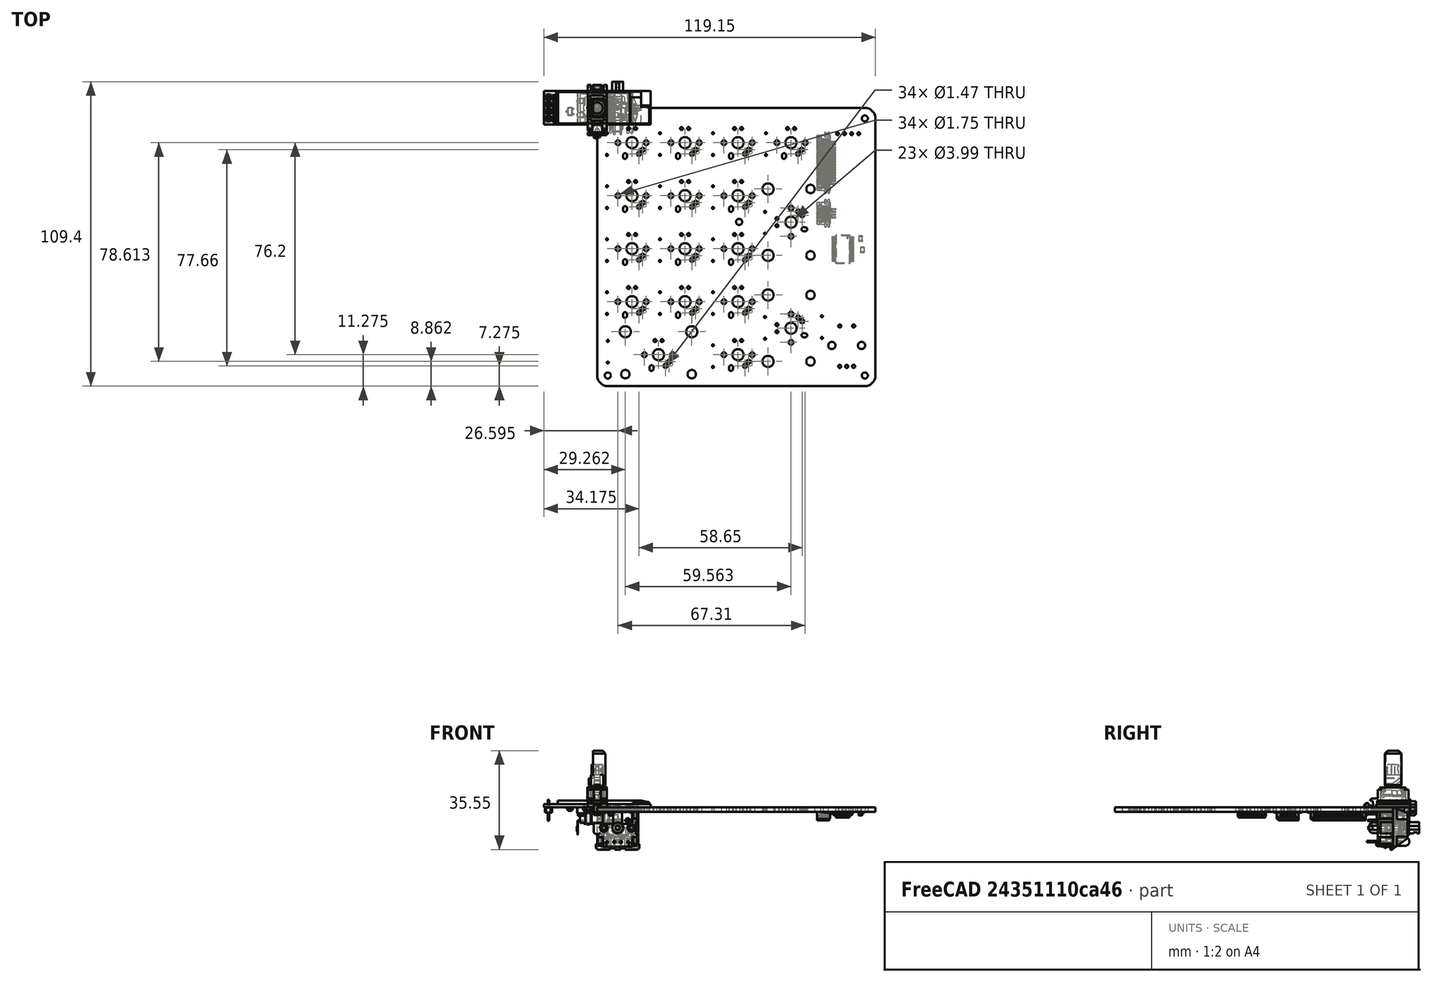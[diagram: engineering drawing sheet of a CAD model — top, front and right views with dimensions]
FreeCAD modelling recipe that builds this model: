
FCSTD DOCUMENT  (FreeCAD 0.19R24267 (Git))
Label: quartet_matrix_numpad
License: All rights reserved
LicenseURL: http://en.wikipedia.org/wiki/All_rights_reserved
objects: Part::Feature×36, App::Link×36, App::Part×13, PartDesign::CoordinateSystem×1, Sketcher::SketchObject×1
note: 38 computed .brp shape members not serialized (recipe doc carries the construction recipe); baked Part::Feature solids carry a one-line shape summary decoded from their .brp

FEATURE [PartDesign::CoordinateSystem] Local_CS_ec40
  AttacherType = Attacher::AttachEngine3D
FEATURE [Part::Feature] Pcb_ec40
  shape: bbox 100 x 100 x 1.6 mm, 259 faces (baked)
FEATURE [Sketcher::SketchObject] PCB_Sketch_ec40
  FullyConstrained = false
  sketch-geometry (8):
    g0: LineSegment StartX=3.81 StartY=-4e-16 StartZ=0 EndX=96.19 EndY=9.3e-15 EndZ=0
    g1: LineSegment StartX=100 StartY=-3.81 StartZ=0 EndX=100 EndY=-96.19 EndZ=0
    g2: LineSegment StartX=96.19 StartY=-100 StartZ=0 EndX=3.81 EndY=-100 EndZ=0
    g3: LineSegment StartX=-7.5e-15 StartY=-96.19 StartZ=0 EndX=4e-16 EndY=-3.81 EndZ=0
    g4: ArcOfCircle CenterX=3.81 CenterY=-3.81 CenterZ=0 NormalX=0 NormalY=0 NormalZ=1 AngleXU=0 Radius=3.81 StartAngle=1.5708 EndAngle=3.14159
    g5: ArcOfCircle CenterX=3.81 CenterY=-96.19 CenterZ=0 NormalX=0 NormalY=0 NormalZ=1 AngleXU=0 Radius=3.81 StartAngle=3.14159 EndAngle=4.71239
    g6: ArcOfCircle CenterX=96.19 CenterY=-96.19 CenterZ=0 NormalX=0 NormalY=0 NormalZ=1 AngleXU=0 Radius=3.81 StartAngle=4.71239 EndAngle=6.28319
    g7: ArcOfCircle CenterX=96.19 CenterY=-3.81 CenterZ=0 NormalX=0 NormalY=0 NormalZ=1 AngleXU=0 Radius=3.81 StartAngle=0 EndAngle=1.5708
  constraints (8):
    c: Coincident(g3,g5)
    c: Coincident(g3,g4)
    c: Coincident(g2,g5)
    c: Coincident(g0,g4)
    c: Coincident(g2,g6)
    c: Coincident(g0,g7)
    c: Coincident(g1,g6)
    c: Coincident(g1,g7)
FEATURE [App::Part] Board_Geoms_ec40
  Group = -> [Local_CS_ec40,Pcb_ec40,PCB_Sketch_ec40]
  Origin = -> Origin
FEATURE [Part::Feature] Part__Feature  label="MX Top Housing"
  shape: bbox 14.82 x 9.998 x 14.77 mm, 582 faces (baked)
FEATURE [Part::Feature] Part__Feature001  label="MX Bottom Housing"
  Placement = pos=(7.35,-0.2,-7.35) rot=(0,0,1;0rad)
  shape: bbox 15.74 x 12.51 x 15.74 mm, 598 faces (baked)
FEATURE [App::Part] Housing
  Group = -> [Part__Feature,Part__Feature001]
  Origin = -> Origin008
  Placement = pos=(7.35,7.35,6) rot=(0,0.707107,0.707107;3.14159rad)
FEATURE [Part::Feature] Part__Feature002  label="MX Slider"
  Placement = pos=(7.35,2,-7.35) rot=(0,0,1;0rad)
  shape: bbox 8.9 x 10.4 x 5.7 mm, 279 faces (baked)
FEATURE [App::Part] Slider
  Group = -> [Part__Feature002]
  Origin = -> Origin009
  Placement = pos=(7.35,7.35,6) rot=(0,0.707107,0.707107;3.14159rad)
FEATURE [Part::Feature] Part__Feature003  label="MX Pins"
  Placement = pos=(-5.57275,-8.7,12.741) rot=(0,0,1;0rad)
  shape: bbox 7.319 x 6.711 x 2.971 mm, 35 faces, 2 solids (baked)
FEATURE [App::Part] Pins
  Group = -> [Part__Feature003]
  Origin = -> Origin010
  Placement = pos=(7.35,7.35,6) rot=(0,0.707107,0.707107;3.14159rad)
FEATURE [Part::Feature] Part__Feature004  label="MX LED"
  Placement = pos=(7.35,0.5,-12.292) rot=(0,0,1;0rad)
  shape: bbox 3.003 x 15.3 x 3.003 mm, 33 faces, 5 solids (baked)
FEATURE [App::Part] LED
  Group = -> [Part__Feature004]
  Origin = -> Origin011
  Placement = pos=(7.35,7.35,6) rot=(0,0.707107,0.707107;3.14159rad)
FEATURE [App::Part] Switch_v7  label="K_PGUP_0_Switch v7_7FFFFFFF"
  Group = -> [Housing,Slider,Pins,LED]
  Origin = -> Origin012
  Placement = pos=(50.625,-31.575,0) rot=(0,0,1;3.14159rad)
FEATURE [Part::Feature] Shape  label="J2_F519-1A7A1-11016-E200_5FF7934A"
  Placement = pos=(78.966,-12.74,-1.6) rot=(0,0,1;1.5708rad)
  shape: bbox 6.803 x 22 x 3.003 mm, 1188 faces (baked)
FEATURE [Part::Feature] Shape001  label="J2_F519-1A7A1-11004-E200_5FF7934A[2]"
  Placement = pos=(78.966,-24.87,-1.6) rot=(0,0,1;1.5708rad)
  shape: bbox 6.803 x 10 x 3.003 mm, 509 faces (baked)
FEATURE [Part::Feature] Shape002  label="U2_SSOP_28_53x102mm_P065mm_5FF8A5C0"
  Placement = pos=(88.265,-50.8,-1.6) rot=(0,1,0;3.14159rad)
  shape: bbox 7.8 x 10.2 x 2.1 mm, 456 faces (baked)
FEATURE [App::Link] U2_SSOP_28_53x102mm_P065mm_5FF8A5C0_ln_  label="U1_SSOP_28_53x102mm_P065mm_5FF8A58F"
  LinkPlacement = pos=(68.58,-59.69,-1.6) rot=(0.707107,0.707107,0;3.14159rad)
  LinkedObject = -> Shape002
  Placement = pos=(68.58,-59.69,-1.6) rot=(0.707107,0.707107,0;3.14159rad)
FEATURE [Part::Feature] Part__Feature005  label="482020714001"
  shape: bbox 13.75 x 11.7 x 25.9 mm, 186 faces (baked)
FEATURE [Part::Feature] Part__Feature006  label="pin"
  Placement = pos=(7.6,-2.5,-2.5) rot=(0,0,1;1.5708rad)
  shape: bbox 2.15 x 1.5 x 7.2 mm, 14 faces (baked)
FEATURE [Part::Feature] Part__Feature007  label="pin_short"
  Placement = pos=(-7.1,-2.5,-4.7) rot=(0,0,-1;1.5708rad)
  shape: bbox 2.353 x 1.503 x 5.003 mm, 32 faces (baked)
FEATURE [Part::Feature] Part__Feature008  label="contact_plate"
  Placement = pos=(2e-16,0,-5.9) rot=(0,0,-1;1.5708rad)
  shape: bbox 9.516 x 11.61 x 9.056 mm, 134 faces (baked)
FEATURE [Part::Feature] Part__Feature009  label="pin001"
  Placement = pos=(7.6,2.5,-2.5) rot=(0,0,1;1.5708rad)
  shape: bbox 2.15 x 1.5 x 7.2 mm, 14 faces (baked)
FEATURE [Part::Feature] Part__Feature010  label="pin002"
  Placement = pos=(7.6,-1.04e-14,-2.5) rot=(0,0,1;1.5708rad)
  shape: bbox 2.15 x 1.5 x 7.2 mm, 14 faces (baked)
FEATURE [Part::Feature] Part__Feature011  label="pin_short001"
  Placement = pos=(-7.1,2.5,-4.7) rot=(0,0,-1;1.5708rad)
  shape: bbox 2.353 x 1.503 x 5.003 mm, 32 faces (baked)
FEATURE [App::Part] _820xx514001_v1  label="SW1_4820xx514001 v1_5FF8A8AA"
  Group = -> [Part__Feature005,Part__Feature006,Part__Feature007,Part__Feature008,Part__Feature009,Part__Feature010,Part__Feature011]
  Origin = -> Origin013
  Placement = pos=(89.67,-85.4,6) rot=(0,0,-1;1.5708rad)
FEATURE [Part::Feature] Shape003  label="R12_R_0805_2012Metric_5FF8A528"
  Placement = pos=(95.25,-51.045,-1.6) rot=(-0.707107,0.707107,0;3.14159rad)
  shape: bbox 1.2 x 2 x 0.45 mm, 26 faces (baked)
FEATURE [App::Link] R12_R_0805_2012Metric_5FF8A528_ln_  label="R11_R_0805_2012Metric_5FF8A517"
  LinkPlacement = pos=(90.424,-21.336,-1.6) rot=(1,0,0;3.14159rad)
  LinkedObject = -> Shape003
  Placement = pos=(90.424,-21.336,-1.6) rot=(1,0,0;3.14159rad)
FEATURE [App::Link] R12_R_0805_2012Metric_5FF8A528_ln_001  label="R10_R_0805_2012Metric_5FF8A506"
  LinkPlacement = pos=(90.424,-19.304,-1.6) rot=(1,0,0;3.14159rad)
  LinkedObject = -> Shape003
  Placement = pos=(90.424,-19.304,-1.6) rot=(1,0,0;3.14159rad)
FEATURE [App::Link] R12_R_0805_2012Metric_5FF8A528_ln_002  label="R9_R_0805_2012Metric_5FF8A4F5"
  LinkPlacement = pos=(90.433,-17.272,-1.6) rot=(1,0,0;3.14159rad)
  LinkedObject = -> Shape003
  Placement = pos=(90.433,-17.272,-1.6) rot=(1,0,0;3.14159rad)
FEATURE [App::Link] R12_R_0805_2012Metric_5FF8A528_ln_003  label="R8_R_0805_2012Metric_5FF8A4E4"
  LinkPlacement = pos=(90.433,-15.24,-1.6) rot=(1,0,0;3.14159rad)
  LinkedObject = -> Shape003
  Placement = pos=(90.433,-15.24,-1.6) rot=(1,0,0;3.14159rad)
FEATURE [App::Link] R12_R_0805_2012Metric_5FF8A528_ln_004  label="R7_R_0805_2012Metric_5FF8A4D3"
  LinkPlacement = pos=(71.628,-51.807,-1.6) rot=(0.707107,0.707107,0;3.14159rad)
  LinkedObject = -> Shape003
  Placement = pos=(71.628,-51.807,-1.6) rot=(0.707107,0.707107,0;3.14159rad)
FEATURE [App::Link] R12_R_0805_2012Metric_5FF8A528_ln_005  label="R6_R_0805_2012Metric_5FF8A4C2"
  LinkPlacement = pos=(69.596,-51.807,-1.6) rot=(0.707107,0.707107,0;3.14159rad)
  LinkedObject = -> Shape003
  Placement = pos=(69.596,-51.807,-1.6) rot=(0.707107,0.707107,0;3.14159rad)
FEATURE [App::Link] R12_R_0805_2012Metric_5FF8A528_ln_006  label="R5_R_0805_2012Metric_5FF8A4B1"
  LinkPlacement = pos=(67.564,-51.807,-1.6) rot=(0.707107,0.707107,0;3.14159rad)
  LinkedObject = -> Shape003
  Placement = pos=(67.564,-51.807,-1.6) rot=(0.707107,0.707107,0;3.14159rad)
FEATURE [App::Link] R12_R_0805_2012Metric_5FF8A528_ln_007  label="R4_R_0805_2012Metric_5FF8A4A0"
  LinkPlacement = pos=(65.532,-51.816,-1.6) rot=(0.707107,0.707107,0;3.14159rad)
  LinkedObject = -> Shape003
  Placement = pos=(65.532,-51.816,-1.6) rot=(0.707107,0.707107,0;3.14159rad)
FEATURE [App::Link] R12_R_0805_2012Metric_5FF8A528_ln_008  label="R3_R_0805_2012Metric_5FF917EF"
  LinkPlacement = pos=(67.056,-67.047,-1.6) rot=(0.707107,0.707107,0;3.14159rad)
  LinkedObject = -> Shape003
  Placement = pos=(67.056,-67.047,-1.6) rot=(0.707107,0.707107,0;3.14159rad)
FEATURE [App::Link] R12_R_0805_2012Metric_5FF8A528_ln_009  label="R2_R_0805_2012Metric_5FF8A47E"
  LinkPlacement = pos=(97.536,-91.431,0) rot=(0,0,1;1.5708rad)
  LinkedObject = -> Shape003
  Placement = pos=(97.536,-91.431,0) rot=(0,0,1;1.5708rad)
FEATURE [App::Link] R12_R_0805_2012Metric_5FF8A528_ln_010  label="R1_R_0805_2012Metric_5FF8A46D"
  LinkPlacement = pos=(81.788,-91.957,0) rot=(0,0,-1;1.5708rad)
  LinkedObject = -> Shape003
  Placement = pos=(81.788,-91.957,0) rot=(0,0,-1;1.5708rad)
FEATURE [Part::Feature] Shape004  label="C4_C_0805_2012Metric_5FF89E4F"
  Placement = pos=(94.615,-46.99,-1.6) rot=(-0.707107,0.707107,0;3.14159rad)
  shape: bbox 1.25 x 2 x 1.25 mm, 28 faces (baked)
FEATURE [App::Link] C4_C_0805_2012Metric_5FF89E4F_ln_  label="C3_C_0805_2012Metric_5FF90FF2"
  LinkPlacement = pos=(96.647,-46.99,-1.6) rot=(-0.707107,0.707107,0;3.14159rad)
  LinkedObject = -> Shape004
  Placement = pos=(96.647,-46.99,-1.6) rot=(-0.707107,0.707107,0;3.14159rad)
FEATURE [App::Link] C4_C_0805_2012Metric_5FF89E4F_ln_001  label="C2_C_0805_2012Metric_5FF9E241"
  LinkPlacement = pos=(71.12,-67.047,-1.6) rot=(0.707107,0.707107,0;3.14159rad)
  LinkedObject = -> Shape004
  Placement = pos=(71.12,-67.047,-1.6) rot=(0.707107,0.707107,0;3.14159rad)
FEATURE [App::Link] C4_C_0805_2012Metric_5FF89E4F_ln_002  label="C1_C_0805_2012Metric_5FF9E2B4"
  LinkPlacement = pos=(69.088,-67.047,-1.6) rot=(0.707107,0.707107,0;3.14159rad)
  LinkedObject = -> Shape004
  Placement = pos=(69.088,-67.047,-1.6) rot=(0.707107,0.707107,0;3.14159rad)
FEATURE [App::Part] Bot_ec40
  Group = -> [Shape,Shape001,Shape002,U2_SSOP_28_53x102mm_P065mm_5FF8A5C0_ln_,Shape003,R12_R_0805_2012Metric_5FF8A528_ln_,R12_R_0805_2012Metric_5FF8A528_ln_001,R12_R_0805_2012Metric_5FF8A528_ln_002,R12_R_0805_2012Metric_5FF8A528_ln_003,R12_R_0805_2012Metric_5FF8A528_ln_004,R12_R_0805_2012Metric_5FF8A528_ln_005,R12_R_0805_2012Metric_5FF8A528_ln_006,R12_R_0805_2012Metric_5FF8A528_ln_007,+5 more]
  Origin = -> Origin004
FEATURE [Part::Feature] Part__Feature012  label="OLED_0.91_128x32.stp"
  shape: bbox 38.3 x 12.1 x 2.57 mm, 270 faces (baked)
FEATURE [Part::Feature] Part__Feature013  label="RESC-0603.stp"
  Placement = pos=(4.3,-5.3,0) rot=(1,0,0;3.14159rad)
  shape: bbox 1.7 x 0.9 x 0.55 mm, 52 faces, 3 solids (baked)
FEATURE [Part::Feature] Part__Feature014  label="RESC-0603.stp001"
  Placement = pos=(4.3,-3.8,0) rot=(1,0,0;3.14159rad)
  shape: bbox 1.7 x 0.9 x 0.55 mm, 52 faces, 3 solids (baked)
FEATURE [Part::Feature] Part__Feature015  label="RESC-0603.stp002"
  Placement = pos=(4.3,-2.3,0) rot=(1,0,0;3.14159rad)
  shape: bbox 1.7 x 0.9 x 0.55 mm, 52 faces, 3 solids (baked)
FEATURE [Part::Feature] Part__Feature016  label="RESC-0603.stp003"
  Placement = pos=(4.3,-0.8,0) rot=(1,0,0;3.14159rad)
  shape: bbox 1.7 x 0.9 x 0.55 mm, 52 faces, 3 solids (baked)
FEATURE [Part::Feature] Part__Feature017  label="RESC-0603.stp004"
  Placement = pos=(4.3,0.7,0) rot=(1,0,0;3.14159rad)
  shape: bbox 1.7 x 0.9 x 0.55 mm, 52 faces, 3 solids (baked)
FEATURE [Part::Feature] Part__Feature018  label="RESC-0603.stp005"
  Placement = pos=(4.3,2.2,0) rot=(1,0,0;3.14159rad)
  shape: bbox 1.7 x 0.9 x 0.55 mm, 52 faces, 3 solids (baked)
FEATURE [Part::Feature] Part__Feature019  label="RESC-0603.stp006"
  Placement = pos=(4.3,3.7,0) rot=(1,0,0;3.14159rad)
  shape: bbox 1.7 x 0.9 x 0.55 mm, 52 faces, 3 solids (baked)
FEATURE [Part::Feature] Part__Feature020  label="RESC-0603.stp007"
  Placement = pos=(4.3,5.2,0) rot=(1,0,0;3.14159rad)
  shape: bbox 1.7 x 0.9 x 0.55 mm, 52 faces, 3 solids (baked)
FEATURE [Part::Feature] Part__Feature021  label="RESC-0603.stp008"
  Placement = pos=(-1.4,-3.06,0) rot=(1,0,0;3.14159rad)
  shape: bbox 1.7 x 0.9 x 0.55 mm, 52 faces, 3 solids (baked)
FEATURE [Part::Feature] Part__Feature022  label="RESC-0603.stp009"
  Placement = pos=(-1.4,-1.56,0) rot=(1,0,0;3.14159rad)
  shape: bbox 1.7 x 0.9 x 0.55 mm, 52 faces, 3 solids (baked)
FEATURE [Part::Feature] Part__Feature023  label="RESC-0603.stp010"
  Placement = pos=(-1.4,-0.06,0) rot=(1,0,0;3.14159rad)
  shape: bbox 1.7 x 0.9 x 0.55 mm, 52 faces, 3 solids (baked)
FEATURE [Part::Feature] Part__Feature024  label="RESC-0603.stp011"
  Placement = pos=(-1.4,1.44,0) rot=(1,0,0;3.14159rad)
  shape: bbox 1.7 x 0.9 x 0.55 mm, 52 faces, 3 solids (baked)
FEATURE [Part::Feature] Part__Feature025  label="RESC-0603.stp012"
  Placement = pos=(-1.4,2.94,0) rot=(1,0,0;3.14159rad)
  shape: bbox 1.7 x 0.9 x 0.55 mm, 52 faces, 3 solids (baked)
FEATURE [Part::Feature] Part__Feature026  label="2SD0601A.stp"
  Placement = pos=(-9.8,-1.3,-0.08) rot=(-1,0,0;1.5708rad)
  shape: bbox 2.759 x 2.9 x 1.18 mm, 55 faces, 4 solids (baked)
FEATURE [Part::Feature] Part__Feature027  label="pcb_connector_350-80-104-00-019101"
  Placement = pos=(-17.55,1.9e-15,-0.06) rot=(0.57735,0.57735,-0.57735;4.18879rad)
  shape: bbox 2.54 x 10.16 x 7.644 mm, 74 faces (baked)
FEATURE [App::Part] SSD1306_OLED_0_91_128x32_SHORT_HEADER_v2  label="A1_SSD1306_OLED_0.91_128x32_SHORT_HEADER v2_5FF7990D"
  Group = -> [Part__Feature012,Part__Feature013,Part__Feature014,Part__Feature015,Part__Feature016,Part__Feature017,Part__Feature018,Part__Feature019,Part__Feature020,Part__Feature021,Part__Feature022,Part__Feature023,Part__Feature024,Part__Feature025,Part__Feature026,Part__Feature027]
  Origin = -> Origin014
  Placement = pos=(90.185,-26.78,1.9) rot=(0,0,-1;1.5708rad)
FEATURE [App::Link] K_PGUP_0_Switch_v7_7FFFFFFF_ln_  label="K_UP_0_PGUP_0_Switch v7_7FFFFFFF"
  LinkPlacement = pos=(31.575,-31.575,0) rot=(0,0,1;3.14159rad)
  LinkedObject = -> Switch_v7
  Placement = pos=(31.575,-31.575,0) rot=(0,0,1;3.14159rad)
FEATURE [App::Link] K_PGUP_0_Switch_v7_7FFFFFFF_ln_001  label="K_SLASH_0_PGUP_0_Switch v7_7FFFFFFF"
  LinkPlacement = pos=(31.575,-12.525,0) rot=(0,0,1;3.14159rad)
  LinkedObject = -> Switch_v7
  Placement = pos=(31.575,-12.525,0) rot=(0,0,1;3.14159rad)
FEATURE [App::Link] K_PGUP_0_Switch_v7_7FFFFFFF_ln_002  label="K_RIGHT_0_PGUP_0_Switch v7_7FFFFFFF"
  LinkPlacement = pos=(50.625,-50.625,0) rot=(0,0,1;3.14159rad)
  LinkedObject = -> Switch_v7
  Placement = pos=(50.625,-50.625,0) rot=(0,0,1;3.14159rad)
FEATURE [App::Link] K_PGUP_0_Switch_v7_7FFFFFFF_ln_003  label="K_PGDN_0_PGUP_0_Switch v7_7FFFFFFF"
  LinkPlacement = pos=(50.625,-69.675,0) rot=(0,0,1;3.14159rad)
  LinkedObject = -> Switch_v7
  Placement = pos=(50.625,-69.675,0) rot=(0,0,1;3.14159rad)
FEATURE [App::Link] K_PGUP_0_Switch_v7_7FFFFFFF_ln_004  label="K_NUM_LOCK_0_PGUP_0_Switch v7_7FFFFFFF"
  LinkPlacement = pos=(12.525,-12.525,0) rot=(0,0,1;3.14159rad)
  LinkedObject = -> Switch_v7
  Placement = pos=(12.525,-12.525,0) rot=(0,0,1;3.14159rad)
FEATURE [App::Link] K_PGUP_0_Switch_v7_7FFFFFFF_ln_005  label="K_MINUS_0_PGUP_0_Switch v7_7FFFFFFF"
  LinkPlacement = pos=(69.675,-12.525,0) rot=(0,0,1;3.14159rad)
  LinkedObject = -> Switch_v7
  Placement = pos=(69.675,-12.525,0) rot=(0,0,1;3.14159rad)
FEATURE [App::Link] K_PGUP_0_Switch_v7_7FFFFFFF_ln_006  label="K_LEFT_0_PGUP_0_Switch v7_7FFFFFFF"
  LinkPlacement = pos=(12.525,-50.625,0) rot=(0,0,1;3.14159rad)
  LinkedObject = -> Switch_v7
  Placement = pos=(12.525,-50.625,0) rot=(0,0,1;3.14159rad)
FEATURE [App::Link] K_PGUP_0_Switch_v7_7FFFFFFF_ln_007  label="K_INS_0_PGUP_0_Switch v7_7FFFFFFF"
  LinkPlacement = pos=(22.05,-88.725,0) rot=(0,0,1;3.14159rad)
  LinkedObject = -> Switch_v7
  Placement = pos=(22.05,-88.725,0) rot=(0,0,1;3.14159rad)
FEATURE [Part::Feature] Part__Feature028  label="mx Stabilizer base 16828"
  Placement = pos=(0,-1.1e-15,3.6) rot=(1,0,0;1.5708rad)
  shape: bbox 6.814 x 19.68 x 10.11 mm, 157 faces (baked)
FEATURE [Part::Feature] Part__Feature029  label="mx Stabilizer key 16828"
  Placement = pos=(0,-3.3e-15,11.7) rot=(1,0,0;1.5708rad)
  shape: bbox 4.613 x 8.314 x 11.98 mm, 287 faces (baked)
FEATURE [App::Part] Cherry_MX_Stabilizer_Open_v1  label="K_INS_0_Cherry MX Stabilizer Open v1_7FFFFFFF[2]"
  Group = -> [Part__Feature028,Part__Feature029]
  Origin = -> Origin015
  Placement = pos=(33.988,-88.725,0) rot=(0,0,1;3.14159rad)
FEATURE [App::Link] K_INS_0_Cherry_MX_Stabilizer_Open_v1_7FFFFFFF_2__ln_  label="K_INS_0_INS_0_Cherry MX Stabilizer Open v1_7FFFFFFF[3]"
  LinkPlacement = pos=(10.112,-88.725,0) rot=(0,0,1;3.14159rad)
  LinkedObject = -> Cherry_MX_Stabilizer_Open_v1
  Placement = pos=(10.112,-88.725,0) rot=(0,0,1;3.14159rad)
FEATURE [App::Link] K_PGUP_0_Switch_v7_7FFFFFFF_ln_008  label="K_HOME_0_PGUP_0_Switch v7_7FFFFFFF"
  LinkPlacement = pos=(12.525,-31.575,0) rot=(0,0,1;3.14159rad)
  LinkedObject = -> Switch_v7
  Placement = pos=(12.525,-31.575,0) rot=(0,0,1;3.14159rad)
FEATURE [App::Link] K_PGUP_0_Switch_v7_7FFFFFFF_ln_009  label="K_ENTER_0_PGUP_0_Switch v7_5FF99BDA"
  LinkPlacement = pos=(69.675,-79.2,0) rot=(0,0,-1;1.5708rad)
  LinkedObject = -> Switch_v7
  Placement = pos=(69.675,-79.2,0) rot=(0,0,-1;1.5708rad)
FEATURE [App::Link] K_INS_0_Cherry_MX_Stabilizer_Open_v1_7FFFFFFF_2__ln_001  label="K_ENTER_0_INS_0_Cherry MX Stabilizer Open v1_5FF99BDA[2]"
  LinkPlacement = pos=(69.675,-67.262,0) rot=(0,0,-1;1.5708rad)
  LinkedObject = -> Cherry_MX_Stabilizer_Open_v1
  Placement = pos=(69.675,-67.262,0) rot=(0,0,-1;1.5708rad)
FEATURE [App::Link] K_INS_0_Cherry_MX_Stabilizer_Open_v1_7FFFFFFF_2__ln_002  label="K_ENTER_0_INS_0_Cherry MX Stabilizer Open v1_5FF99BDA[3]"
  LinkPlacement = pos=(69.675,-91.138,0) rot=(0,0,-1;1.5708rad)
  LinkedObject = -> Cherry_MX_Stabilizer_Open_v1
  Placement = pos=(69.675,-91.138,0) rot=(0,0,-1;1.5708rad)
FEATURE [App::Link] K_PGUP_0_Switch_v7_7FFFFFFF_ln_010  label="K_END_0_PGUP_0_Switch v7_7FFFFFFF"
  LinkPlacement = pos=(12.525,-69.675,0) rot=(0,0,1;3.14159rad)
  LinkedObject = -> Switch_v7
  Placement = pos=(12.525,-69.675,0) rot=(0,0,1;3.14159rad)
FEATURE [App::Link] K_PGUP_0_Switch_v7_7FFFFFFF_ln_011  label="K_DOWN_0_PGUP_0_Switch v7_7FFFFFFF"
  LinkPlacement = pos=(31.575,-69.675,0) rot=(0,0,1;3.14159rad)
  LinkedObject = -> Switch_v7
  Placement = pos=(31.575,-69.675,0) rot=(0,0,1;3.14159rad)
FEATURE [App::Link] K_PGUP_0_Switch_v7_7FFFFFFF_ln_012  label="K_DEL_0_PGUP_0_Switch v7_7FFFFFFF"
  LinkPlacement = pos=(50.625,-88.725,0) rot=(0,0,1;3.14159rad)
  LinkedObject = -> Switch_v7
  Placement = pos=(50.625,-88.725,0) rot=(0,0,1;3.14159rad)
FEATURE [App::Link] K_PGUP_0_Switch_v7_7FFFFFFF_ln_013  label="K_5_0_PGUP_0_Switch v7_7FFFFFFF"
  LinkPlacement = pos=(31.575,-50.625,0) rot=(0,0,1;3.14159rad)
  LinkedObject = -> Switch_v7
  Placement = pos=(31.575,-50.625,0) rot=(0,0,1;3.14159rad)
FEATURE [App::Link] K_PGUP_0_Switch_v7_7FFFFFFF_ln_014  label="K_+_0_PGUP_0_Switch v7_7FFFFFFF"
  LinkPlacement = pos=(69.675,-41.1,0) rot=(0,0,-1;1.5708rad)
  LinkedObject = -> Switch_v7
  Placement = pos=(69.675,-41.1,0) rot=(0,0,-1;1.5708rad)
FEATURE [App::Link] K_INS_0_Cherry_MX_Stabilizer_Open_v1_7FFFFFFF_2__ln_003  label="K_+_0_INS_0_Cherry MX Stabilizer Open v1_7FFFFFFF[2]"
  LinkPlacement = pos=(69.675,-29.162,0) rot=(0,0,-1;1.5708rad)
  LinkedObject = -> Cherry_MX_Stabilizer_Open_v1
  Placement = pos=(69.675,-29.162,0) rot=(0,0,-1;1.5708rad)
FEATURE [App::Link] K_INS_0_Cherry_MX_Stabilizer_Open_v1_7FFFFFFF_2__ln_004  label="K_+_0_INS_0_Cherry MX Stabilizer Open v1_7FFFFFFF[3]"
  LinkPlacement = pos=(69.675,-53.038,0) rot=(0,0,-1;1.5708rad)
  LinkedObject = -> Cherry_MX_Stabilizer_Open_v1
  Placement = pos=(69.675,-53.038,0) rot=(0,0,-1;1.5708rad)
FEATURE [App::Link] K_PGUP_0_Switch_v7_7FFFFFFF_ln_015  label="REF_K_PGUP_0_Switch v7_7FFFFFFF"
  LinkPlacement = pos=(50.625,-12.525,0) rot=(0,0,1;3.14159rad)
  LinkedObject = -> Switch_v7
  Placement = pos=(50.625,-12.525,0) rot=(0,0,1;3.14159rad)
FEATURE [App::Part] Top_ec40
  Group = -> [Switch_v7,_820xx514001_v1,R12_R_0805_2012Metric_5FF8A528_ln_009,R12_R_0805_2012Metric_5FF8A528_ln_010,SSD1306_OLED_0_91_128x32_SHORT_HEADER_v2,K_PGUP_0_Switch_v7_7FFFFFFF_ln_,K_PGUP_0_Switch_v7_7FFFFFFF_ln_001,K_PGUP_0_Switch_v7_7FFFFFFF_ln_002,K_PGUP_0_Switch_v7_7FFFFFFF_ln_003,K_PGUP_0_Switch_v7_7FFFFFFF_ln_004,K_PGUP_0_Switch_v7_7FFFFFFF_ln_005,K_PGUP_0_Switch_v7_7FFFFFFF_ln_006,+15 more]
  Origin = -> Origin003
FEATURE [App::Part] Step_Models_ec40
  Group = -> [Top_ec40,Bot_ec40]
  Origin = -> Origin002
FEATURE [App::Part] Board_ec40  label="quartet_matrix_numpad"
  Group = -> [Board_Geoms_ec40,Step_Models_ec40]
  Origin = -> Origin001
